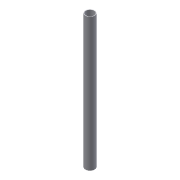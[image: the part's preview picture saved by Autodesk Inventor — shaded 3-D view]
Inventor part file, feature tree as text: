
AUTODESK INVENTOR PART (.ipt)
format: ipt  version: 2015 (Build 190159000, 159)  size: 116,224 bytes
history: native  units: mm
features: sketch x2, other x1, extrude x1, shell x1, hole x1
ambient origin geometry x8: Origin, YZ Plane, XZ Plane, XY Plane, X Axis, Y Axis, Z Axis, Center Point
bodies: Body1 (feature_tree)
feature tree (6):
  other  "Bryła2"
  extrude  "Wyciągnięcie proste2"  Depth=32.0mm
  shell  "Skorupa2"  Thickness=460.0mm
  hole  "Otwór1"  [1 undecoded]
  sketch  "Szkic2"
  sketch  "Szkic3"
note: 1 required parameter value undecoded (feature->parameter linkage not recoverable at this tier; creation-order binding heuristic only, values carry confidence <= 0.55)
